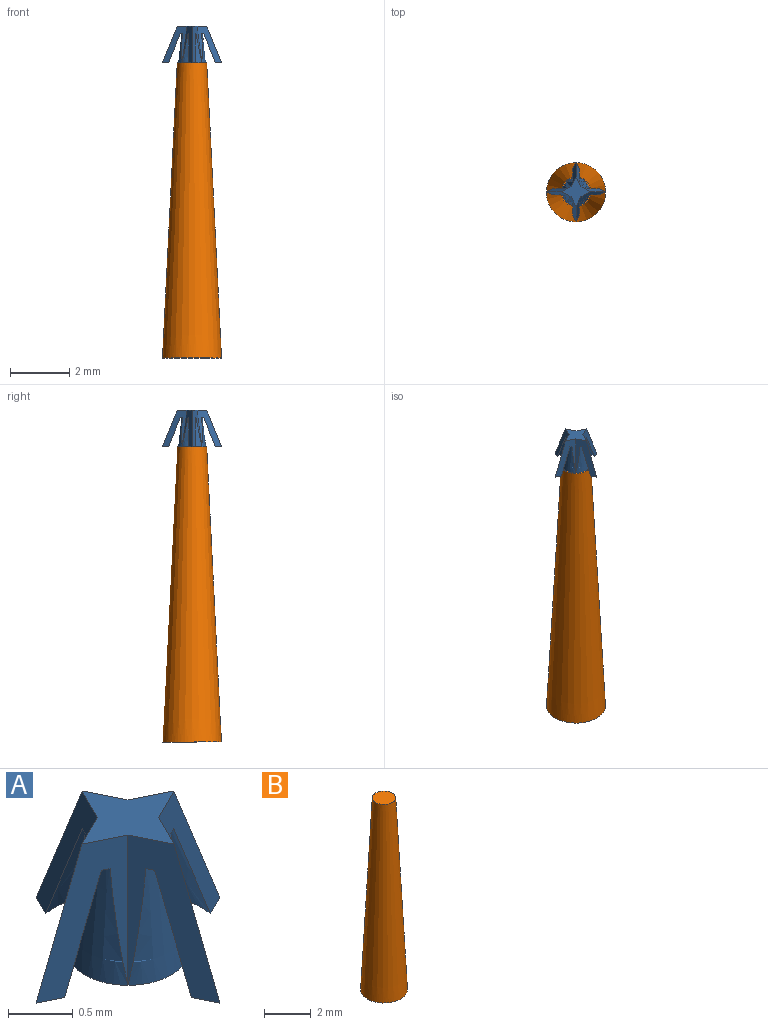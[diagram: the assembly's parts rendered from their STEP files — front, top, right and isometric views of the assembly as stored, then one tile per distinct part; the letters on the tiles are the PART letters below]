
ASSEMBLY  parts=2 mates=1
PART A: 26 faces, bbox 2.1x2.1x1.4 mm
  f0: plane 1.36x0.94mm, normal (0.44,-0.88,0.18), area 0.4mm2, adj f1,f2,f4,f5,f6,f7,f10
  f1: plane 0.21x0.21mm, normal (0,0,-1), area 0mm2, adj f0,f2,f5
  f2: plane 1.36x0.94mm, normal (0.44,0.88,0.18), area 0.4mm2, adj f0,f1,f4,f5,f6,f7,f11
  f3: plane 0.94x0.94mm, normal (0,0,-1), area 0.7mm2, adj f7,f8,f9,f16
  f4: plane 1x1mm, normal (0,0,1), area 0.3mm2, adj f0,f2,f10,f11,f12,f17,f18,f22
  f5: cone r=0.41mm half-angle=21.5deg, axis (0,0,-1), area 0.2mm2, adj f0,f1,f2,f6
  f6: plane 0.27x0.08mm, normal (0,0,-1), area 0mm2, adj f0,f2,f5,f7
  f7: cone r=0.47mm half-angle=6.5deg, axis (0,0,-1), area 0.5mm2, adj f0,f2,f3,f6
  f8: cone r=0.47mm half-angle=6.5deg, axis (0,0,-1), area 0.5mm2, adj f3,f10,f12,f15
  f9: cone r=0.47mm half-angle=6.5deg, axis (0,0,-1), area 0.5mm2, adj f3,f11,f22,f25
  f10: plane 1.36x0.94mm, normal (0.88,-0.44,0.18), area 0.4mm2, adj f0,f4,f8,f12,f13,f14,f15
  f11: plane 1.36x0.94mm, normal (0.88,0.44,0.18), area 0.4mm2, adj f2,f4,f9,f22,f23,f24,f25
  f12: plane 1.36x0.94mm, normal (-0.88,-0.44,0.18), area 0.4mm2, adj f4,f8,f10,f13,f14,f15,f17
  f13: plane 0.21x0.21mm, normal (0,0,-1), area 0mm2, adj f10,f12,f14
  f14: cone r=0.41mm half-angle=21.5deg, axis (0,0,-1), area 0.2mm2, adj f10,f12,f13,f15
  f15: plane 0.27x0.08mm, normal (0,0,-1), area 0mm2, adj f8,f10,f12,f14
  f16: cone r=0.47mm half-angle=6.5deg, axis (0,0,-1), area 0.5mm2, adj f3,f17,f18,f21
  f17: plane 1.36x0.94mm, normal (-0.44,-0.88,0.18), area 0.4mm2, adj f4,f12,f16,f18,f19,f20,f21
  f18: plane 1.36x0.94mm, normal (-0.44,0.88,0.18), area 0.4mm2, adj f4,f16,f17,f19,f20,f21,f22
  f19: plane 0.21x0.21mm, normal (0,0,-1), area 0mm2, adj f17,f18,f20
  f20: cone r=0.41mm half-angle=21.5deg, axis (0,0,-1), area 0.2mm2, adj f17,f18,f19,f21
  f21: plane 0.27x0.08mm, normal (0,0,-1), area 0mm2, adj f16,f17,f18,f20
  f22: plane 1.36x0.94mm, normal (-0.88,0.44,0.18), area 0.4mm2, adj f4,f9,f11,f18,f23,f24,f25
  f23: plane 0.21x0.21mm, normal (0,0,-1), area 0mm2, adj f11,f22,f24
  f24: cone r=0.41mm half-angle=21.5deg, axis (0,0,-1), area 0.2mm2, adj f11,f22,f23,f25
  f25: plane 0.27x0.08mm, normal (0,0,-1), area 0mm2, adj f9,f11,f22,f24
PART B: 3 faces, bbox 2x2x10 mm
  f0: plane 2x2mm, normal (0,0,-1), area 3.1mm2, adj f1
  f1: cone r=0.5mm half-angle=2.9deg, axis (0,0,-1), area 47.2mm2, adj f0,f2
  f2: plane 1x1mm, normal (0,0,1), area 0.8mm2, adj f1
PLACE A at identity
PLACE B t=(0,0,-10)mm
MATE fastened A.f5 <-> B.f1  axis (0,0,-1) through (0,0,0)mm
